# Revit family: 00e7d020-5f29-47d1-b6b5-b1afe3fbaff5
name_source: partatom
category: Furniture
revit_build: Autodesk Revit 2016 (Build: 20161004_0715(x64)
units: mm (PartAtom-declared; Revit-internal decimal feet)

## family parameters
Cut with Voids When Loaded = No
Host = Face
OmniClass Number = 23.40.95.00
OmniClass Title = Furnishings, Ornaments, and Decoration
Room Calculation Point = No
Shared = No

## types (3) — shared parameters
Art Note = Frame 37x31 uses 16x20 Image, Frame 31x39 uses 20x30 Image, Frame 35x45 uses 24x36 Image
Default Elevation = 54"
Depth = 1 1/8"
Description = Ligature Resistant Art Frame
Frame Finish = Wood-BSP-Cherry
Front Protection Finish = Polycarbonate-BSP-Clear
Manufacturer = Behavioral Safety Products
Mat Finish = Paper-BSP-White Mat
Model = AF550
Product Documentation Link = http://besafeprod.com
Product Page URL = http://besafeprod.com
Type Image = <None>
URL = http://besafeprod.com

## per-type parameters (varying)
| type | Art Selection | Height | Image Height | Image Width | Width |
| 35" x 45" | Image-41 : 24x36 | 35" | 24" | 36" | 45" |
| 31" x 39" | Image-41 : 20x30 | 31" | 20" | 30" | 39" |
| 27" x 31" | Image-41 : 16x20 | 27" | 16" | 20" | 31" |

## geometry (parser evidence)
native form markers: Blend x98, Sweep x27
no freeform markers — native parametric forms only
